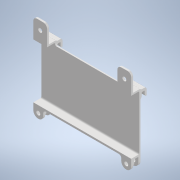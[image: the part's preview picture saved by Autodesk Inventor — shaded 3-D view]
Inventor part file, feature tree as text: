
AUTODESK INVENTOR PART (.ipt)
format: ipt  version: 2022 (Build 260153000, 153)  size: 554,496 bytes
history: native  units: mm
features: reference x23, fillet x11, other x9, extrude x8, sketch x8, projected_geometry x8, chamfer x2, mirror x1
ambient origin geometry x8: Origin, YZ Plane, XZ Plane, XY Plane, X Axis, Y Axis, Z Axis, Center Point
bodies: Body1 (feature_tree)
feature tree (70):
  other  "Твердое тело1"
  extrude  "Выдавливание1"  Depth=1.5mm
  extrude  "Выдавливание2"  Depth=2.0mm TaperAngle=0.0deg
  other  "РабПлоскость1"
  extrude  "Выдавливание3"  Depth=2.0mm TaperAngle=0.0deg
  fillet  "Сопряжение1"  Radius=6.452mm
  extrude  "Выдавливание4"  Depth=0.3mm
  fillet  "Сопряжение2"  Radius=1.0mm
  fillet  "Сопряжение3"  Radius=1.5mm
  other  "РабПлоскость2"
  extrude  "Выдавливание7"  Depth=3.2mm
  chamfer  "Фаска2"  Distance=3.2mm
  fillet  "Сопряжение5"  Radius=3.0mm
  fillet  "Сопряжение6"  Radius=1.0mm
  extrude  "Выдавливание9"  Depth=1.952mm TaperAngle=0.0deg
  fillet  "Сопряжение7"  Radius=1.0mm
  fillet  "Сопряжение8"  Radius=1.5mm
  extrude  "Выдавливание10"  Depth=8.0mm
  chamfer  "Фаска3"  Distance=3.2mm
  extrude  "Выдавливание11"  Depth=3.2mm
  fillet  "Сопряжение9"  Radius=6.0mm
  fillet  "Сопряжение10"  Radius=6.0mm
  fillet  "Сопряжение11"  Radius=1.0mm
  mirror  "Зеркальное отражение1"
  fillet  "Сопряжение12"  Radius=1.7mm
  sketch  "Эскиз1"
  reference  "Ссылка1"
  reference  "Ссылка2"
  reference  "Ссылка3"
  sketch  "Эскиз2"
  projected_geometry  "Спроецированная петля1"
  sketch  "Эскиз3"
  projected_geometry  "Спроецированная петля2"
  reference  "Ссылка4"
  reference  "Ссылка5"
  reference  "Ссылка6"
  reference  "Ссылка7"
  reference  "Ссылка8"
  reference  "Ссылка9"
  sketch  "Эскиз4"
  reference  "Ссылка10"
  reference  "Ссылка11"
  projected_geometry  "Спроецированная петля3"
  reference  "Ссылка12"
  reference  "Ссылка13"
  reference  "Ссылка14"
  reference  "Ссылка15"
  reference  "Ссылка16"
  reference  "Ссылка19"
  sketch  "Эскиз7"
  projected_geometry  "Спроецированная петля4"
  projected_geometry  "Спроецированная петля5"
  sketch  "Эскиз9"
  projected_geometry  "Спроецированная петля6"
  projected_geometry  "Спроецированная петля7"
  sketch  "Эскиз10"
  projected_geometry  "Спроецированная петля8"
  sketch  "Эскиз11"
  reference  "Ссылка20"
  reference  "Ссылка21"
  reference  "Ссылка22"
  reference  "Ссылка23"
  reference  "Ссылка24"
  reference  "Ссылка25"
  other  "<userpath>\Documents\Git\MZCAT_2024\MZCAT_3.iam"
  other  "MZCAT_3.iam"
  other  "commutationCATboard:1"
  other  "CAT_protector:1"
  other  "vydacha_slide:1"
  other  "base plate:2"
